# Revit family: Mixer_Kitchen_Nero_Mecca_Sensor_PullOut
name_source: partatom
category: Plumbing Fixtures
units: mm (PartAtom-declared; Revit-internal decimal feet)

## family parameters
Always vertical = Yes
Cut with Voids When Loaded = Yes
Maintain Annotation Orientation = No
OmniClass Number = 23.31.11.19
OmniClass Title = Faucet Mixing Valves
Part Type = Normal
Room Calculation Point = No
Round Connector Dimension = Use Diameter
Shared = No
Work Plane-Based = No

## types (7) — shared parameters
Assembly Code = D2010
CW Connection = Yes
Default Elevation = 900 mm
HW Connection = Yes
IfcExportAs = IfcValveType
IfcExportType = FAUCET
Manufacturer = Nero
ManufacturerOverallDepth = 260.3 mm  [stored 0.854003 ft]
ManufacturerOverallHeight = 438 mm  [stored 1.43701 ft]
ManufacturerOverallWidth = 111.9 mm  [stored 0.367126 ft]
ManufacturerURLProductSpecific = https://pleaseloadfromtypecatalog.com
ModifiedIssue = 20251105 $
URL = https://nerotapware.com.au
Uniclass2015Code = Pr_40_20_87
Uniclass2015Title = Taps and water supply outlet fittings
Uniclass2015Version = Products v1.35
Vent Connection = No
Waste Connection = No
zero-valued in all types: CWFU, HWFU, WFU

## per-type parameters (varying)
| type | Description | ManufacturerSpecCode | Material | Model | Type Comments |
| Matte White (NR221908aMW) | Mecca Smart Sensor Pull Out Kitchen Mixer Matte white | NR221908aMW | Metal_MatteWhite_Nero | NR221908aMW | Mixer - Kitchen - Sensor - Pull Out - Matte White |
| Matte Black (NR221908aMB) | Mecca Smart Sensor Pull Out Kitchen Mixer Matte Black | NR221908aMB | Metal_MatteBlack_Nero | NR221908aMB | Mixer - Kitchen - Sensor - Pull Out - Matte Black |
| Brushed Gold (NR221908aBG) | Mecca Smart Sensor Pull Out Kitchen Mixer Brushed Gold | NR221908aBG | Metal_Gold_Nero_Brushed | NR221908aBG | Mixer - Kitchen - Sensor - Pull Out - Brushed Gold |
| Brushed Bronze (NR221908aBZ) | Mecca Smart Sensor Pull Out Kitchen Mixer Brushed Bronze | NR221908aBZ | Metal_Bronze_Nero_Brushed | NR221908aBZ | Mixer - Kitchen - Sensor - Pull Out - Brushed Bronze |
| Brushed Nickel (NR221908aBN) | Mecca Smart Sensor Pull Out Kitchen Mixer Brushed Nickel | NR221908aBN | Metal_Nickel_Nero_Brushed | NR221908aBN | Mixer - Kitchen - Sensor - Pull Out - Brushed Nickel |
| Gunmetal (NR221908aGM) | Mecca Smart Sensor Pull Out Kitchen Mixer Gun Metal | NR221908aGM | Metal_GunMetal_Nero | NR221908aGM | Mixer - Kitchen - Sensor - Pull Out - Gunmetal |
| Chrome (NR221908aCH) | Mecca Smart Sensor Pull Out Kitchen Mixer Chrome | NR221908aCH | Metal_Chrome_Nero | NR221908aCH | Mixer - Kitchen - Sensor - Pull Out - Chrome |

note: [stored X ft] marks values corroborated as IEEE doubles in the binary element streams (Revit-internal decimal feet)

## geometry (parser evidence)
native form markers: Sweep x2
no freeform markers — native parametric forms only
